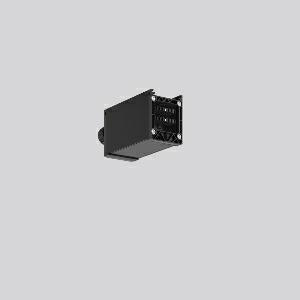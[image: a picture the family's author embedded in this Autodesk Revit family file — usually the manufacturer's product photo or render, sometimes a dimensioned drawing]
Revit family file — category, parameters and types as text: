
# Revit family: linedo_anfangseinspeisung_982859_003_d6cf
name_source: partatom
category: Lighting Fixtures
units: mm (PartAtom-declared; Revit-internal decimal feet)

## family parameters
Cut with Voids When Loaded = No
Host = Face
Light Source = No
Part Type = Normal
Room Calculation Point = No
Round Connector Dimension = Use Diameter
Shared = No

## types (1)
- LINEDO Anfangseinspeisung
    Apparent Load = 0 VA
    Default Elevation = 1800 mm
    Description = Series: LINEDO
Initial power feed (short Version), 7-pole, connection socket. Housing: extruded aluminium profile, powder-coated. Cover made of plastic, surface like housing. LINEDO plug system, plastic, black. 1 cable gland (M25). Cable gland on side or on top. Convenient connection with flat connector.
Colour: black
Length: 134 mm
Width: 58 mm
Height: 76 mm
Weight: 278 g
    Height = 76 mm
    Lamp = 0 x
    Length = 134 mm
    Luminous efficacy = 0 lm/W
    Manufacturer = RZB
    ModVariant = No
    Model = 982859.003
    Mounting Place = Ceiling
    Mounting Type = Surface mounted
    Number of Poles = 1
    OnlyDefault = Yes
    Power Factor = 1
    Product Name = LINEDO Anfangseinspeisung
    Product group = Continuous line luminaire system Linedo IP 54
    ProductGroupID = 314
    Protection Class = Protection class I
    Protection Degree = Degree of protection
    RLX_Detail_Level = 1
    RLX_Emergency_Light_Flux = 0 lm
    RLX_Emergency_Type = 0
    RLX_Emergency_Type_DB = No
    RlxData = <blob elided: 14037 chars, md5=16fe0814>
    Standby Power = 0 W
    System Light Flux = 0 lm
    System Power = 0 W
    Type Comments = Product without accessories
    Type Image = 982859.003.jpg
    URL = http://relux.com
    VarID = ---
    Voltage = 0 V
    Weight = 0.00 kg
    Width = 58 mm

## geometry (parser evidence)
native form markers: Sweep x8
no freeform markers — native parametric forms only
